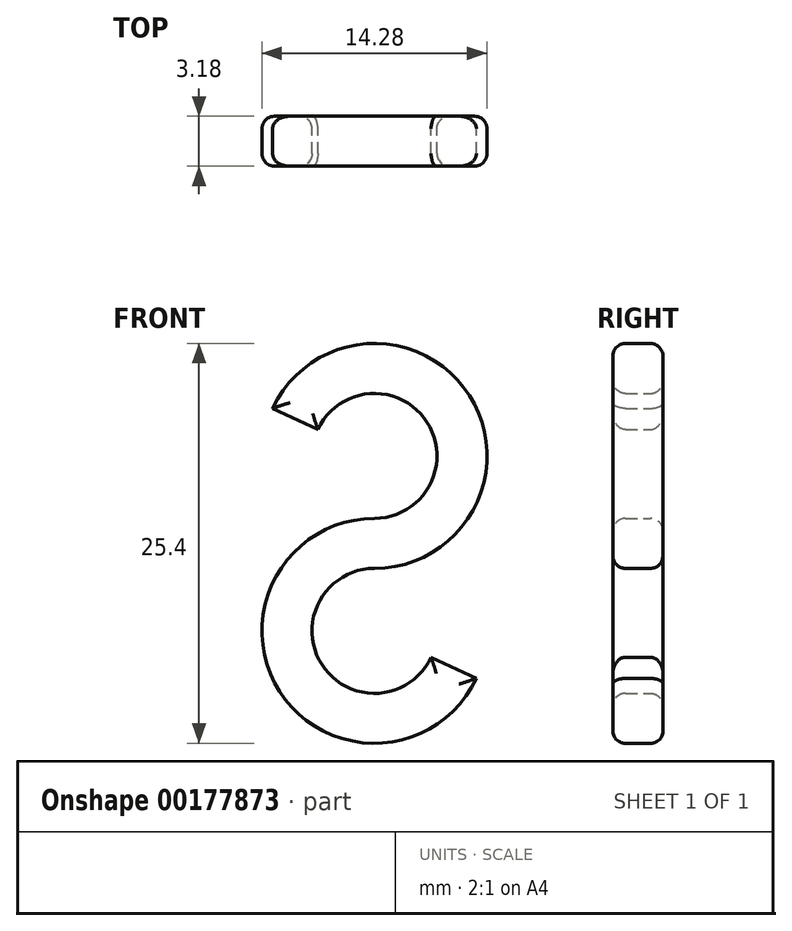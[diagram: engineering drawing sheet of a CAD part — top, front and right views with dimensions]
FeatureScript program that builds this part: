
annotation { "Feature Type Name" : "Feature", "Feature Type Description" : "" }
export const myFeature = defineFeature(function(context is Context, id is Id, definition is map)
    precondition{}
    {
        {
            var Q0;
            Q0=qCreatedBy(makeId("Front.planeOp"),FACE);
            var sketch = newSketch(context, id + "F0", { "sketchPlane" : qUnion([Q0])});
            skArc(sketch, "E0", {"start": v(0, 7.14) * mm, "mid": v(3.35, 13.24) * mm, "end": v(-3.6, 12.79) * mm});
            skArc(sketch, "E1", {"start": v(0, 3.97) * mm, "mid": v(-3.35, -2.13) * mm, "end": v(3.6, -1.68) * mm});
            skArc(sketch, "E2", {"start": v(0, 3.97) * mm, "mid": v(6.02, 14.95) * mm, "end": v(-6.47, 14.13) * mm});
            skArc(sketch, "E3", {"start": v(0, 7.14) * mm, "mid": v(-6.02, -3.84) * mm, "end": v(6.47, -3.02) * mm});
            skLineSegment(sketch, "E4", {"start": v(-3.6, 12.79) * mm, "end": v(-6.47, 14.13) * mm});
            skLineSegment(sketch, "E5", {"start": v(3.6, -1.68) * mm, "end": v(6.47, -3.02) * mm});
            skSolve(sketch);
        }
        {
            var Q0;
            Q0 = qSketchRegion(id + "F0", true);
            extrude(context, id + "F1", {"entities" : qUnion([Q0]), "depth" : 3.17 * mm});
        }
        {
            var Q0;
            Q0=makeQuery(id+"F1.opExtrude","CAP_FACE",FACE,{"disambiguationData":[OSD([sQuery(id+"F0.wireOp",EDGE,"E0"),sQuery(id+"F0.wireOp",EDGE,"E1"),sQuery(id+"F0.wireOp",EDGE,"E2"),sQuery(id+"F0.wireOp",EDGE,"E3"),sQuery(id+"F0.wireOp",EDGE,"E4"),sQuery(id+"F0.wireOp",EDGE,"E5")])],"isStart":false});
            var Q1;
            Q1=makeQuery(id+"F1.opExtrude","CAP_FACE",FACE,{"disambiguationData":[OSD([sQuery(id+"F0.wireOp",EDGE,"E0"),sQuery(id+"F0.wireOp",EDGE,"E1"),sQuery(id+"F0.wireOp",EDGE,"E2"),sQuery(id+"F0.wireOp",EDGE,"E3"),sQuery(id+"F0.wireOp",EDGE,"E4"),sQuery(id+"F0.wireOp",EDGE,"E5")])],"isStart":true});
            fillet(context, id + "F2", {"entities" : qUnion([Q0, Q1]), "radius" : 0.8 * mm, "tangentPropagation" : true, "allowEdgeOverflow" : false});
        }
    });
